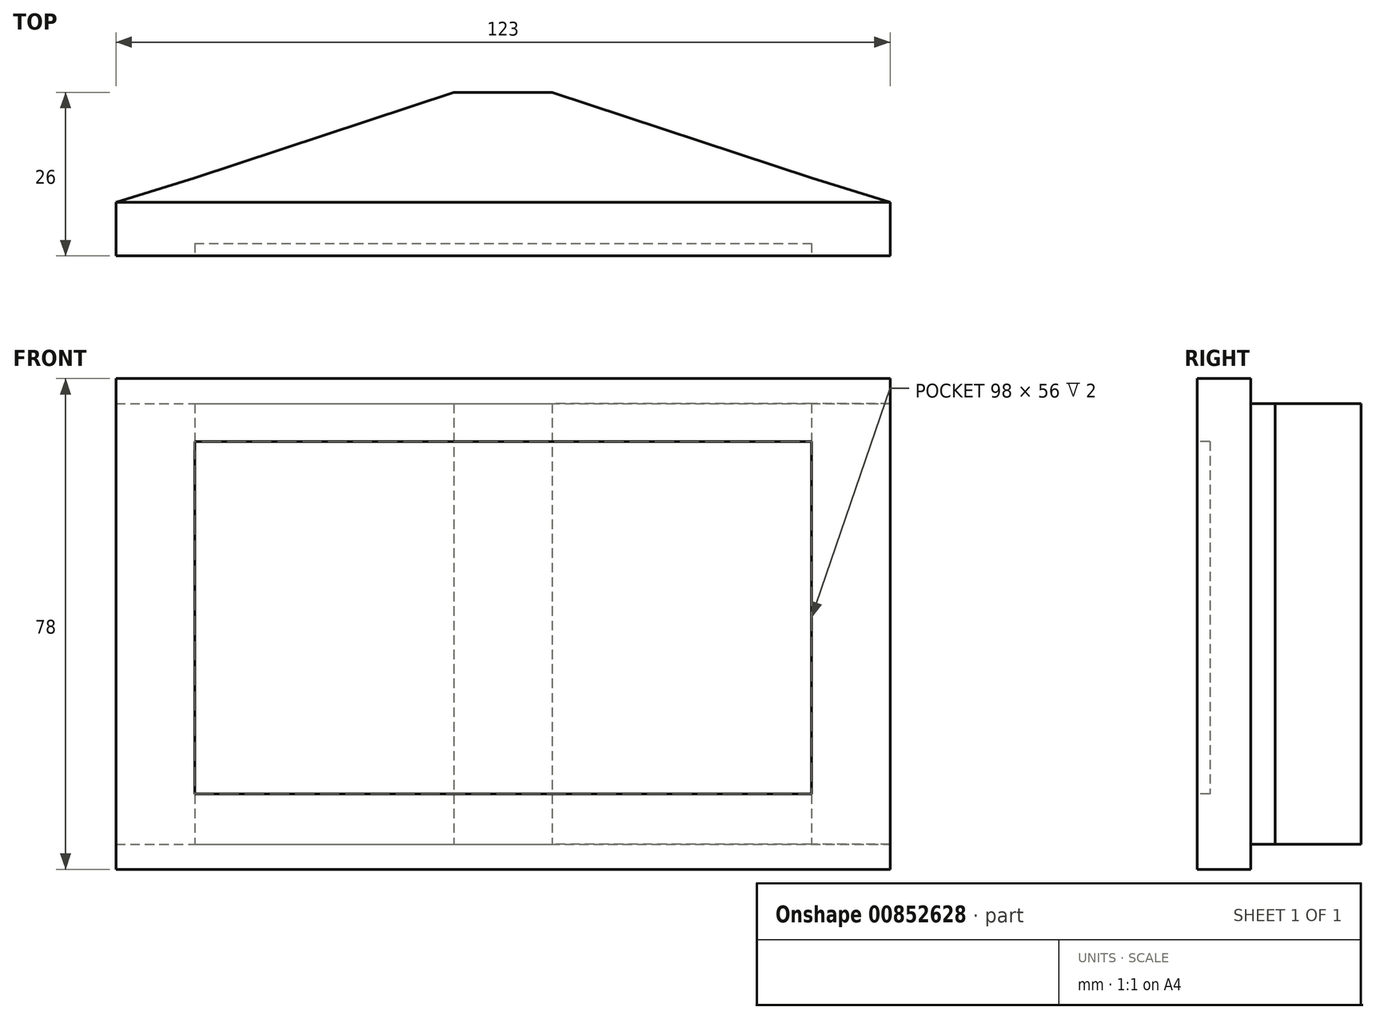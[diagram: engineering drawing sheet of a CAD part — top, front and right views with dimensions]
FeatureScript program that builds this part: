
annotation { "Feature Type Name" : "Feature", "Feature Type Description" : "" }
export const myFeature = defineFeature(function(context is Context, id is Id, definition is map)
    precondition{}
    {
        {
            var Q0;
            Q0=qCreatedBy(makeId("Front.planeOp"),FACE);
            var sketch = newSketch(context, id + "F0", { "sketchPlane" : qUnion([Q0])});
            skLineSegment(sketch, "E0.bottom", {"start": v(-61.5, -39) * mm, "end": v(61.5, -39) * mm});
            skLineSegment(sketch, "E0.top", {"start": v(-61.5, 39) * mm, "end": v(61.5, 39) * mm});
            skLineSegment(sketch, "E0.left", {"start": v(-61.5, -39) * mm, "end": v(-61.5, 39) * mm});
            skLineSegment(sketch, "E0.right", {"start": v(61.5, -39) * mm, "end": v(61.5, 39) * mm});
            skSolve(sketch);
        }
        {
            var Q0;
            Q0 = qSketchRegion(id + "F0", true);
            extrude(context, id + "F1", {"entities" : qUnion([Q0]), "oppositeDirection" : true, "depth" : 8.5 * mm, "offsetDistance" : 25 * mm});
        }
        {
            var Q0;
            Q0=makeQuery(id+"F1.opExtrude","CAP_FACE",FACE,{"disambiguationData":[OSD([sQuery(id+"F0.wireOp",EDGE,"E0.bottom"),sQuery(id+"F0.wireOp",EDGE,"E0.top"),sQuery(id+"F0.wireOp",EDGE,"E0.left"),sQuery(id+"F0.wireOp",EDGE,"E0.right")])],"isStart":true});
            var sketch = newSketch(context, id + "F2", { "sketchPlane" : qUnion([Q0])});
            skLineSegment(sketch, "E1.bottom", {"start": v(-49, 29) * mm, "end": v(49, 29) * mm});
            skLineSegment(sketch, "E1.top", {"start": v(-49, -27) * mm, "end": v(49, -27) * mm});
            skLineSegment(sketch, "E1.left", {"start": v(-49, 29) * mm, "end": v(-49, -27) * mm});
            skLineSegment(sketch, "E1.right", {"start": v(49, 29) * mm, "end": v(49, -27) * mm});
            skSolve(sketch);
        }
        {
            var Q0;
            Q0 = qSketchRegion(id + "F2", true);
            extrude(context, id + "F3", {"entities" : qUnion([Q0]), "operationType" : NewBodyOperationType.REMOVE, "oppositeDirection" : true, "depth" : 2 * mm, "offsetDistance" : 25 * mm});
        }
        {
            var Q0;
            Q0=qCreatedBy(makeId("Top.planeOp"),FACE);
            var sketch = newSketch(context, id + "F4", { "sketchPlane" : qUnion([Q0])});
            skLineSegment(sketch, "E2", {"start": v(-61.5, 8.5) * mm, "end": v(-49, 12.4) * mm});
            skLineSegment(sketch, "E3", {"start": v(-49, 12.4) * mm, "end": v(-7.8, 26) * mm});
            skLineSegment(sketch, "E4", {"start": v(-7.8, 26) * mm, "end": v(0, 26) * mm});
            skLineSegment(sketch, "E5", {"start": v(0, 41.72) * mm, "end": v(0, -20.22) * mm, "construction": true});
            skLineSegment(sketch, "E6.MirrorCS", {"start": v(61.5, 8.5) * mm, "end": v(49, 12.4) * mm});
            skLineSegment(sketch, "E7.MirrorCS", {"start": v(49, 12.4) * mm, "end": v(7.8, 26) * mm});
            skLineSegment(sketch, "E8.MirrorCS", {"start": v(7.8, 26) * mm, "end": v(0, 26) * mm});
            skLineSegment(sketch, "E9.0", {"start": v(-61.5, 8.5) * mm, "end": v(61.5, 8.5) * mm});
            skSolve(sketch);
        }
        {
            var Q0;
            Q0 = qSketchRegion(id + "F4", true);
            extrude(context, id + "F5", {"entities" : qUnion([Q0]), "operationType" : NewBodyOperationType.ADD, "depth" : 35 * mm, "offsetDistance" : 25 * mm, "hasSecondDirection" : true, "secondDirectionOppositeDirection" : true, "secondDirectionDepth" : 35 * mm});
        }
    });
